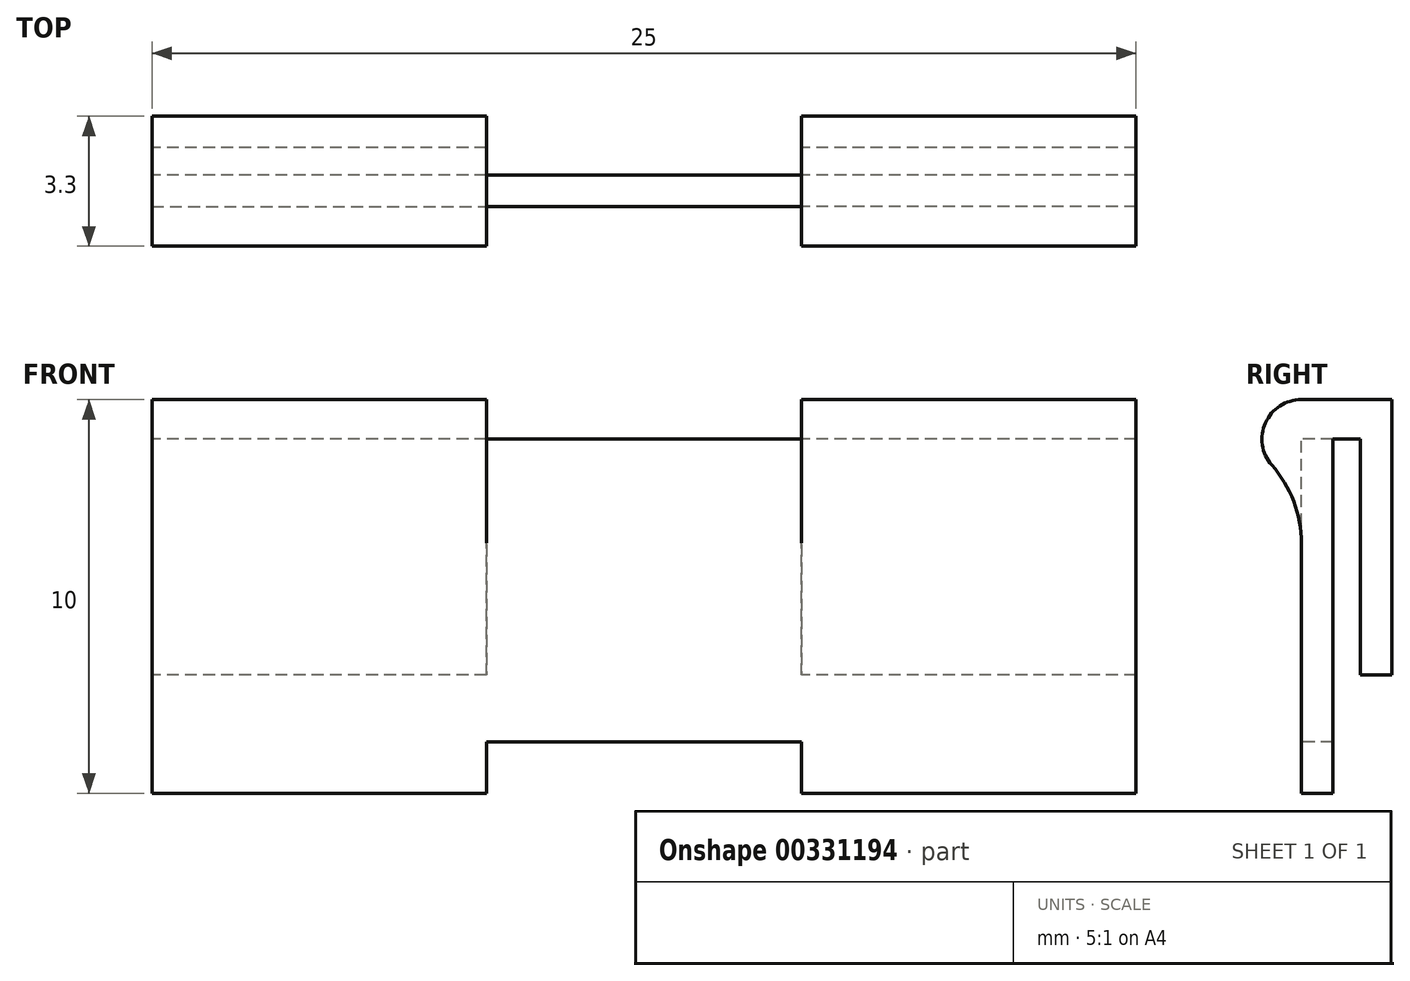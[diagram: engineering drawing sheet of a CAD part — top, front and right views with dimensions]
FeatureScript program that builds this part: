
annotation { "Feature Type Name" : "Feature", "Feature Type Description" : "" }
export const myFeature = defineFeature(function(context is Context, id is Id, definition is map)
    precondition{}
    {
        {
            var Q0;
            Q0=qCreatedBy(makeId("Right.planeOp"),FACE);
            var sketch = newSketch(context, id + "F0", { "sketchPlane" : qUnion([Q0])});
            skLineSegment(sketch, "E0", {"start": v(2.3, 0) * mm, "end": v(0, 0) * mm});
            skLineSegment(sketch, "E1", {"start": v(0, -10) * mm, "end": v(0.8, -10) * mm});
            skLineSegment(sketch, "E2", {"start": v(0.8, -10) * mm, "end": v(0.8, -1) * mm});
            skLineSegment(sketch, "E3", {"start": v(0.8, -1) * mm, "end": v(1.5, -1) * mm});
            skLineSegment(sketch, "E4", {"start": v(2.3, -7) * mm, "end": v(2.3, 0) * mm});
            skLineSegment(sketch, "E5", {"start": v(1.5, -1) * mm, "end": v(1.5, -7) * mm});
            skLineSegment(sketch, "E6", {"start": v(1.5, -7) * mm, "end": v(2.3, -7) * mm});
            skArc(sketch, "E7", {"start": v(0, 0) * mm, "mid": v(-1, -1) * mm, "end": v(0, -2) * mm});
            skLineSegment(sketch, "E8.trimOffspring", {"start": v(0, -2) * mm, "end": v(0, -10) * mm});
            skSolve(sketch);
        }
        {
            var Q0;
            Q0 = qSketchRegion(id + "F0", true);
            extrude(context, id + "F1", {"entities" : qUnion([Q0]), "endBound" : BoundingType.SYMMETRIC, "depth" : 25 * mm});
        }
        {
            var Q0;
            Q0=qCreatedBy(makeId("Front.planeOp"),FACE);
            var sketch = newSketch(context, id + "F2", { "sketchPlane" : qUnion([Q0])});
            skLineSegment(sketch, "E9.bottom", {"start": v(-4, 0) * mm, "end": v(4, 0) * mm});
            skLineSegment(sketch, "E9.top", {"start": v(-4, -1) * mm, "end": v(4, -1) * mm});
            skLineSegment(sketch, "E9.left", {"start": v(-4, 0) * mm, "end": v(-4, -1) * mm});
            skLineSegment(sketch, "E9.right", {"start": v(4, 0) * mm, "end": v(4, -1) * mm});
            skLineSegment(sketch, "E10.bottom", {"start": v(-4, -8.7) * mm, "end": v(4, -8.7) * mm});
            skLineSegment(sketch, "E10.top", {"start": v(-4, -10) * mm, "end": v(4, -10) * mm});
            skLineSegment(sketch, "E10.left", {"start": v(-4, -8.7) * mm, "end": v(-4, -10) * mm});
            skLineSegment(sketch, "E10.right", {"start": v(4, -8.7) * mm, "end": v(4, -10) * mm});
            skSolve(sketch);
        }
        {
            var Q0;
            Q0 = qSketchRegion(id + "F2", true);
            extrude(context, id + "F3", {"entities" : qUnion([Q0]), "operationType" : NewBodyOperationType.REMOVE, "endBound" : BoundingType.THROUGH_ALL, "oppositeDirection" : true, "depth" : 25 * mm});
        }
        {
            var Q0;
            Q0=qCreatedBy(makeId("Top.planeOp"),FACE);
            var sketch = newSketch(context, id + "F4", { "sketchPlane" : qUnion([Q0])});
            skLineSegment(sketch, "E11.bottom", {"start": v(-4, 2.3) * mm, "end": v(4, 2.3) * mm});
            skLineSegment(sketch, "E11.top", {"start": v(-4, 1.5) * mm, "end": v(4, 1.5) * mm});
            skLineSegment(sketch, "E11.left", {"start": v(-4, 2.3) * mm, "end": v(-4, 1.5) * mm});
            skLineSegment(sketch, "E11.right", {"start": v(4, 2.3) * mm, "end": v(4, 1.5) * mm});
            skLineSegment(sketch, "E12.bottom", {"start": v(-4, 0) * mm, "end": v(4, 0) * mm});
            skLineSegment(sketch, "E12.top", {"start": v(-4, -1.12) * mm, "end": v(4, -1.12) * mm});
            skLineSegment(sketch, "E12.left", {"start": v(-4, 0) * mm, "end": v(-4, -1.12) * mm});
            skLineSegment(sketch, "E12.right", {"start": v(4, 0) * mm, "end": v(4, -1.12) * mm});
            skSolve(sketch);
        }
        {
            var Q0;
            Q0 = qSketchRegion(id + "F4", true);
            extrude(context, id + "F5", {"entities" : qUnion([Q0]), "operationType" : NewBodyOperationType.REMOVE, "endBound" : BoundingType.THROUGH_ALL, "oppositeDirection" : true, "depth" : 25 * mm});
        }
        {
            var Q0;
            {var subQ0=sQuery(id+"F0.wireOp",EDGE,"E8.trimOffspring");var subQ1=sQuery(id+"F0.wireOp",EDGE,"E7");Q0=makeQuery(id+"F5.boolean.opBoolean","SPLIT",EDGE,{"disambiguationData":[TD([makeQuery(id+"F3.boolean.opBoolean","COPY",FACE,{"derivedFrom":makeQuery(id+"F3.opExtrude","SWEPT_FACE",FACE,{"disambiguationData":[OSD([sQuery(id+"F2.wireOp",EDGE,"E9.left")])]})})])],"derivedFrom":makeQuery(id+"F1.opExtrude","SWEPT_EDGE",EDGE,{"disambiguationData":[OSD([subQ1,subQ0])]})});}
            var Q1;
            {var subQ0=sQuery(id+"F0.wireOp",EDGE,"E8.trimOffspring");var subQ1=sQuery(id+"F0.wireOp",EDGE,"E7");Q1=makeQuery(id+"F5.boolean.opBoolean","SPLIT",EDGE,{"disambiguationData":[TD([makeQuery(id+"F3.boolean.opBoolean","COPY",FACE,{"derivedFrom":makeQuery(id+"F3.opExtrude","SWEPT_FACE",FACE,{"disambiguationData":[OSD([sQuery(id+"F2.wireOp",EDGE,"E9.right")])]})})])],"derivedFrom":makeQuery(id+"F1.opExtrude","SWEPT_EDGE",EDGE,{"disambiguationData":[OSD([subQ1,subQ0])]})});}
            fillet(context, id + "F6", {"entities" : qUnion([Q0, Q1]), "radius" : 3 * mm, "tangentPropagation" : true, "allowEdgeOverflow" : false});
        }
    });
